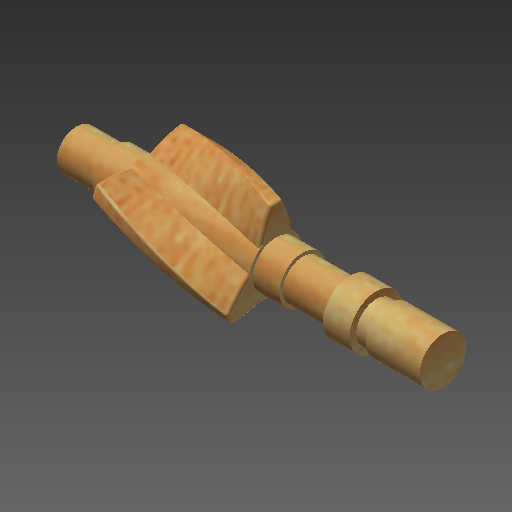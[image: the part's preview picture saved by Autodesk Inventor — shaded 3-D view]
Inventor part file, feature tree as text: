
AUTODESK INVENTOR PART (.ipt)
format: ipt  version: 2020 (Build 240168000, 168)  size: 493,056 bytes
history: native  units: mm
features: extrude x4, fillet x2, other x1, revolve x1, mirror x1, chamfer x1, helix x1, pattern_circular x1
ambient origin geometry x8: Origin, YZ Plane, XZ Plane, XY Plane, X Axis, Y Axis, Z Axis, Center Point
bodies: Body1 (feature_tree)
feature tree (12):
  other  "實體1"
  revolve  "Revolution1"  [1 undecoded]
  mirror  "Mirror1"
  extrude  "Extrusion5"  Depth=5.0mm
  extrude  "Extrusion6"  Depth=1.75mm
  chamfer  "Chamfer4"  Distance=1.5mm
  extrude  "Extrusion8"  Depth=3.0mm
  extrude  "Extrusion9"  TaperAngle=90.0deg  [1 undecoded]
  helix  "Coil4"  [1 undecoded]
  pattern_circular  "Circular Pattern3"  [2 undecoded]
  fillet  "Fillet6"  Radius=4.0mm
  fillet  "Fillet7"  Radius=2.0mm
note: 5 required parameter values undecoded (feature->parameter linkage not recoverable at this tier; creation-order binding heuristic only, values carry confidence <= 0.55)